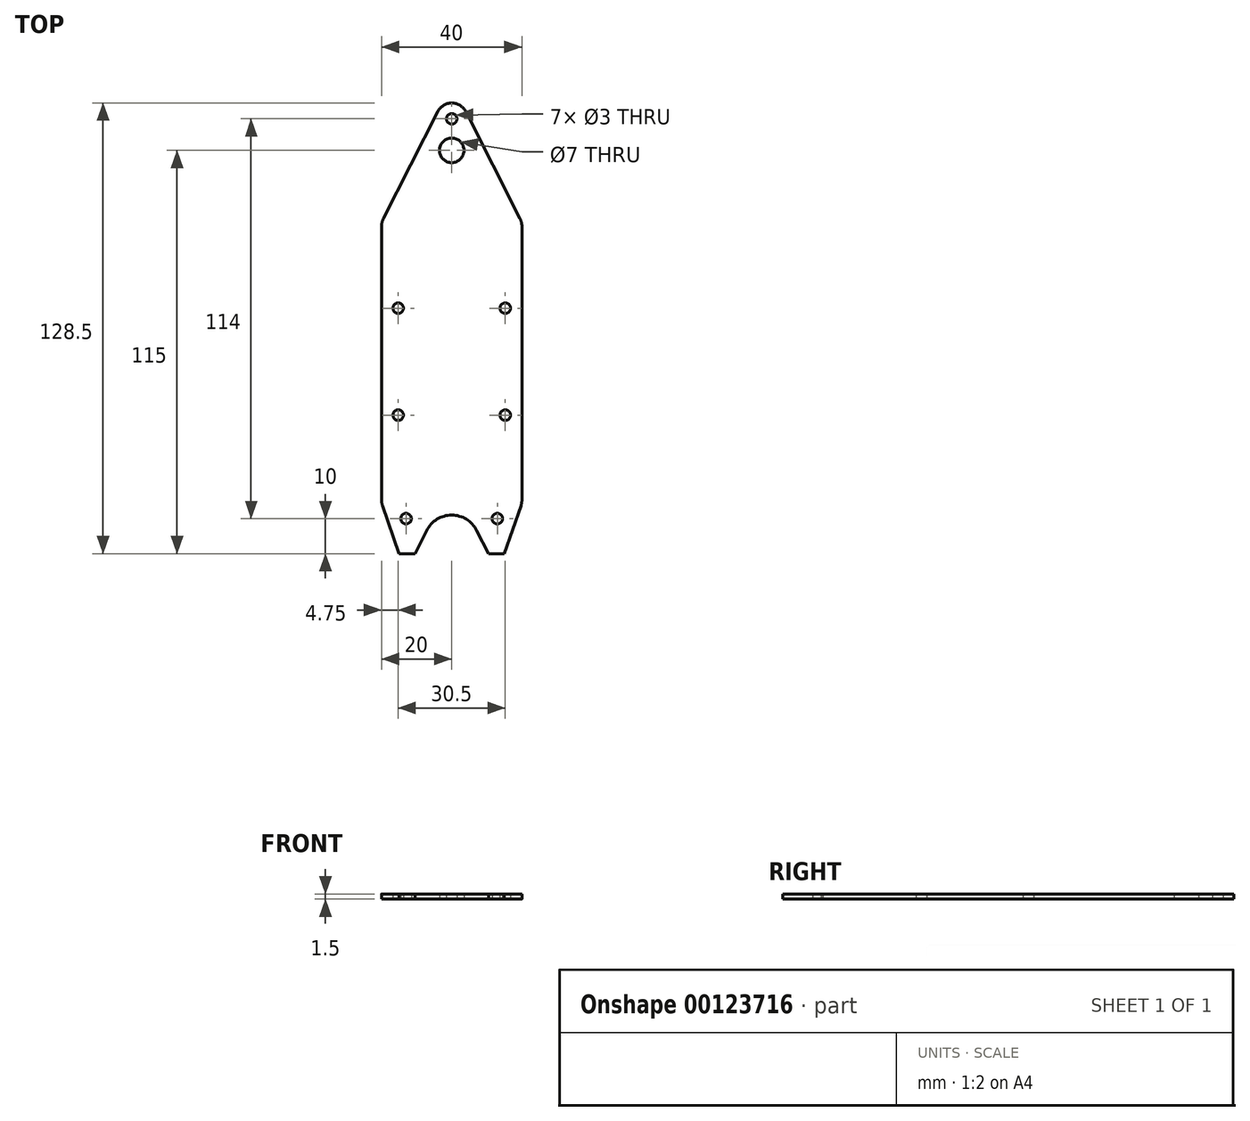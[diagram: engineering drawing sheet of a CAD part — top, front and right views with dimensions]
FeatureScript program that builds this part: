
annotation { "Feature Type Name" : "Feature", "Feature Type Description" : "" }
export const myFeature = defineFeature(function(context is Context, id is Id, definition is map)
    precondition{}
    {
        {
            var Q0;
            Q0=qCreatedBy(makeId("Top.planeOp"),FACE);
            var sketch = newSketch(context, id + "F0", { "sketchPlane" : qUnion([Q0])});
            skCircle(sketch, "E0", {"center": v(0, 69.25) * mm, "radius": 1.5 * mm});
            skArc(sketch, "E1", {"start": v(4.01, 71.28) * mm, "mid": v(0, 73.75) * mm, "end": v(-4.01, 71.28) * mm});
            skCircle(sketch, "E2", {"center": v(-13, -44.75) * mm, "radius": 1.5 * mm});
            skCircle(sketch, "E3", {"center": v(13, -44.75) * mm, "radius": 1.5 * mm});
            skLineSegment(sketch, "E4", {"start": v(-13, -44.75) * mm, "end": v(13, -44.75) * mm, "construction": true});
            skCircle(sketch, "E5", {"center": v(-15.25, 15.25) * mm, "radius": 1.5 * mm});
            skCircle(sketch, "E6.0.1.0", {"center": v(-15.25, -15.25) * mm, "radius": 1.5 * mm});
            skCircle(sketch, "E6.1.0.0", {"center": v(15.25, 15.25) * mm, "radius": 1.5 * mm});
            skCircle(sketch, "E6.1.1.0", {"center": v(15.25, -15.25) * mm, "radius": 1.5 * mm});
            skLineSegment(sketch, "E6.direction1", {"start": v(-15.25, 15.25) * mm, "end": v(15.25, 15.25) * mm, "construction": true});
            skLineSegment(sketch, "E6.direction2", {"start": v(-15.25, 15.25) * mm, "end": v(-15.25, -15.25) * mm, "construction": true});
            skLineSegment(sketch, "E7", {"start": v(-20, 38.56) * mm, "end": v(-20, -39.41) * mm});
            skLineSegment(sketch, "E8", {"start": v(20, 38.56) * mm, "end": v(20, -39.41) * mm});
            skLineSegment(sketch, "E9", {"start": v(-19.46, 40.82) * mm, "end": v(-4.01, 71.28) * mm});
            skLineSegment(sketch, "E10", {"start": v(19.46, 40.82) * mm, "end": v(4.01, 71.28) * mm});
            skLineSegment(sketch, "E11", {"start": v(-19.73, -41.04) * mm, "end": v(-15, -54.75) * mm});
            skLineSegment(sketch, "E12", {"start": v(15, -54.75) * mm, "end": v(19.73, -41.04) * mm});
            skLineSegment(sketch, "E13", {"start": v(-15, -54.75) * mm, "end": v(-10.5, -54.75) * mm});
            skLineSegment(sketch, "E14", {"start": v(15, -54.75) * mm, "end": v(10.5, -54.75) * mm});
            skArc(sketch, "E15", {"start": v(7.13, -48.12) * mm, "mid": v(0, -43.75) * mm, "end": v(-7.13, -48.12) * mm});
            skLineSegment(sketch, "E16", {"start": v(-10.5, -54.75) * mm, "end": v(-7.13, -48.12) * mm});
            skLineSegment(sketch, "E17", {"start": v(10.5, -54.75) * mm, "end": v(7.13, -48.12) * mm});
            skCircle(sketch, "E18", {"center": v(0, 60.25) * mm, "radius": 3.5 * mm});
            skPoint(sketch, "E19.visualSharp", {"position": v(-20, 39.75) * mm});
            skArc(sketch, "E19.filletArc", {"start": v(-19.46, 40.82) * mm, "mid": v(-19.86, 39.72) * mm, "end": v(-20, 38.56) * mm});
            skPoint(sketch, "E20.visualSharp", {"position": v(20, 39.75) * mm});
            skArc(sketch, "E20.filletArc", {"start": v(20, 38.56) * mm, "mid": v(19.86, 39.72) * mm, "end": v(19.46, 40.82) * mm});
            skPoint(sketch, "E21.visualSharp", {"position": v(-20, -40.25) * mm});
            skArc(sketch, "E21.filletArc", {"start": v(-20, -39.41) * mm, "mid": v(-19.93, -40.24) * mm, "end": v(-19.73, -41.04) * mm});
            skPoint(sketch, "E22.visualSharp", {"position": v(20, -40.25) * mm});
            skArc(sketch, "E22.filletArc", {"start": v(19.73, -41.04) * mm, "mid": v(19.93, -40.24) * mm, "end": v(20, -39.41) * mm});
            skLineSegment(sketch, "E23", {"start": v(-15, 38.56) * mm, "end": v(15, 38.56) * mm, "construction": true});
            skSolve(sketch);
        }
        {
            var Q0;
            Q0=qSketchRegion(id+"F0",true);
            extrude(context, id + "F1", {"entities" : qUnion([Q0]), "depth" : 1.5 * mm});
        }
    });
